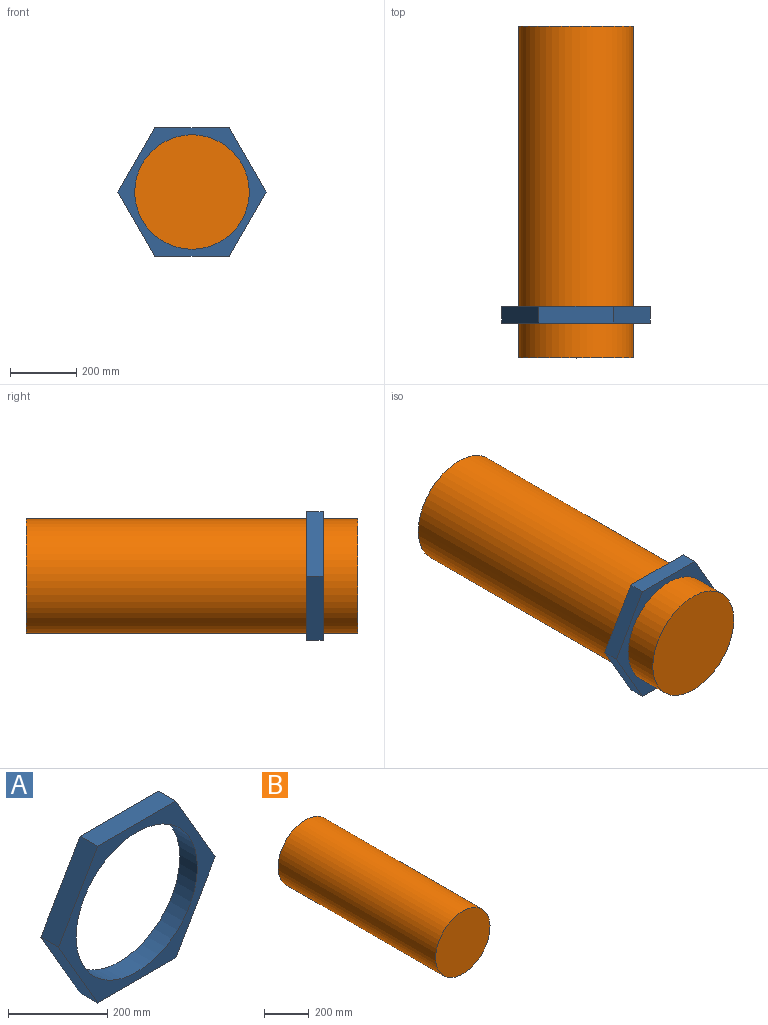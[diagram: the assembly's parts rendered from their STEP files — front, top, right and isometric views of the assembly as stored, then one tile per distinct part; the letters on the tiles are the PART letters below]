
ASSEMBLY  parts=2 mates=1
PART A: 9 faces, bbox 446.2x50x386.4 mm
  f0: plane 193.2x111.55mm, normal (-0.87,0,-0.5), area 11154.7mm2, adj f1,f6,f7,f8
  f1: plane 223.09x50mm, normal (0,0,-1), area 11154.7mm2, adj f0,f2,f7,f8
  f2: plane 193.2x111.55mm, normal (0.87,0,-0.5), area 11154.7mm2, adj f1,f3,f7,f8
  f3: plane 193.2x111.55mm, normal (0.87,0,0.5), area 11154.7mm2, adj f2,f4,f7,f8
  f4: plane 223.09x50mm, normal (0,0,1), area 11154.7mm2, adj f3,f6,f7,f8
  f5: cylinder r=172.5mm len=345mm, axis (0,1,0), area 54192.5mm2, adj f7,f8
  f6: plane 193.2x111.55mm, normal (-0.87,0,0.5), area 11154.7mm2, adj f0,f4,f7,f8
  f7: plane 446.19x386.41mm, normal (0,-1,0), area 35825.8mm2, adj f0,f1,f2,f3,f4,f5,f6
  f8: plane 446.19x386.41mm, normal (0,1,0), area 35825.8mm2, adj f0,f1,f2,f3,f4,f5,f6
PART B: 3 faces, bbox 345x1000x345 mm
  f0: cylinder r=172.5mm len=1000mm, axis (0,1,0), area 1083849.5mm2, adj f1,f2
  f1: plane 345x345mm, normal (0,-1,0), area 93482mm2, adj f0
  f2: plane 345x345mm, normal (0,1,0), area 93482mm2, adj f0
PLACE A t=(70.95,-414.54,-42.47)mm
PLACE B t=(70.95,430.65,-42.47)mm
MATE slider A.f5 <-> B.f0  axis (0,1,0) through (70.95,-439.54,-42.47)mm
